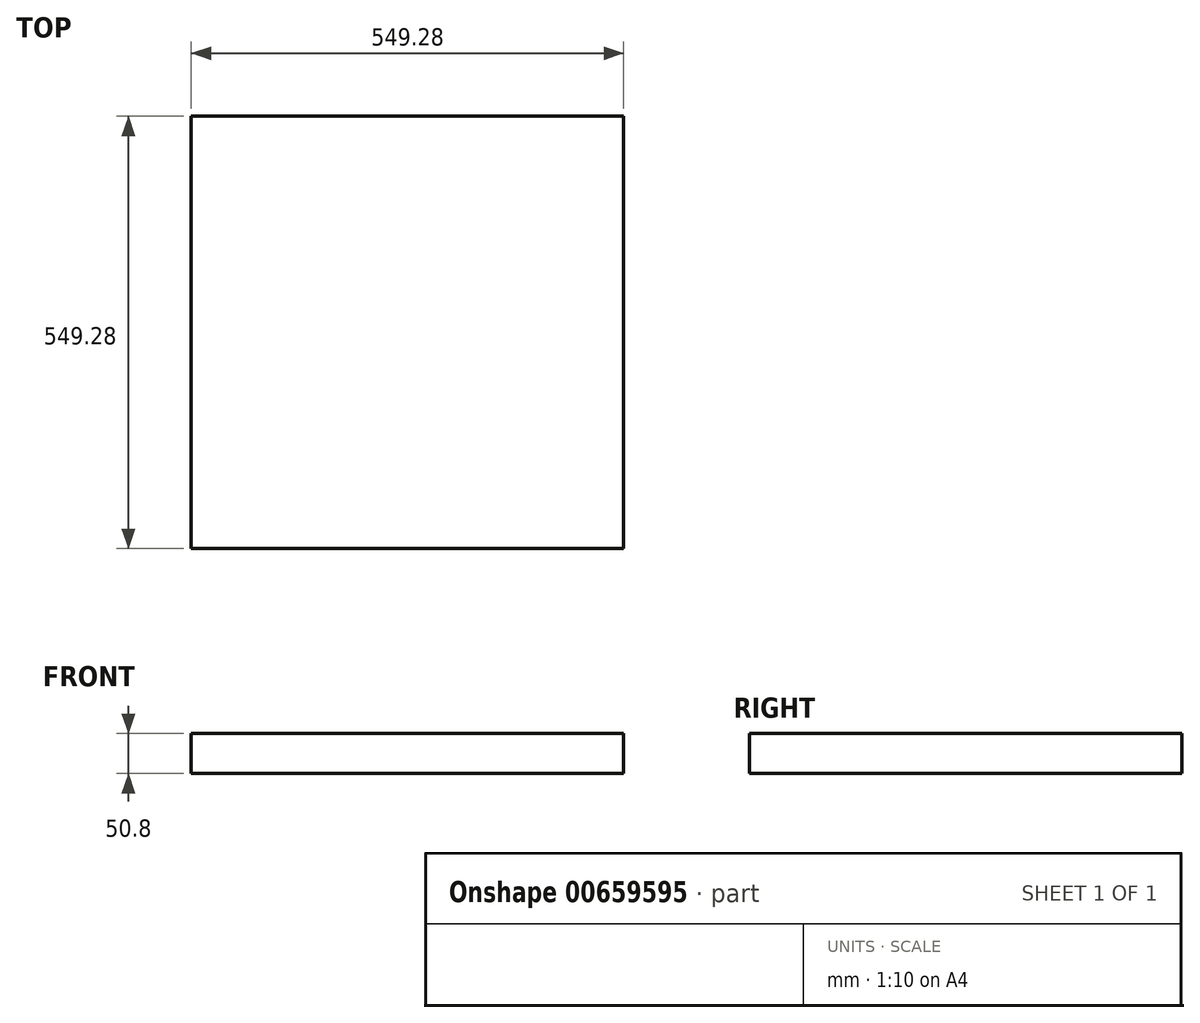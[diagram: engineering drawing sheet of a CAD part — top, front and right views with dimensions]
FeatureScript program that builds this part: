
annotation { "Feature Type Name" : "Feature", "Feature Type Description" : "" }
export const myFeature = defineFeature(function(context is Context, id is Id, definition is map)
    precondition{}
    {
        {
            var Q0;
            Q0=qCreatedBy(makeId("Top.planeOp"),FACE);
            var sketch = newSketch(context, id + "F0", { "sketchPlane" : qUnion([Q0])});
            skLineSegment(sketch, "E0.bottom", {"start": v(274.64, -274.64) * mm, "end": v(-274.64, -274.64) * mm});
            skLineSegment(sketch, "E0.top", {"start": v(274.64, 274.64) * mm, "end": v(-274.64, 274.64) * mm});
            skLineSegment(sketch, "E0.left", {"start": v(274.64, -274.64) * mm, "end": v(274.64, 274.64) * mm});
            skLineSegment(sketch, "E0.right", {"start": v(-274.64, -274.64) * mm, "end": v(-274.64, 274.64) * mm});
            skPoint(sketch, "E0.middle", {"position": v(0, 0) * mm});
            skSolve(sketch);
        }
        {
            var Q0;
            Q0=makeQuery(id+"F0.imprint","IMPRINT",FACE,{"disambiguationData":[TD([[makeQuery(id+"F0.imprint","IMPRINT",EDGE,{"derivedFrom":sQuery(id+"F0.wireOp",EDGE,"E0.bottom")}),-1.0]])]});
            extrude(context, id + "F1", {"entities" : qUnion([Q0]), "depth" : 50.8 * mm, "offsetDistance" : 25 * mm});
        }
    });
